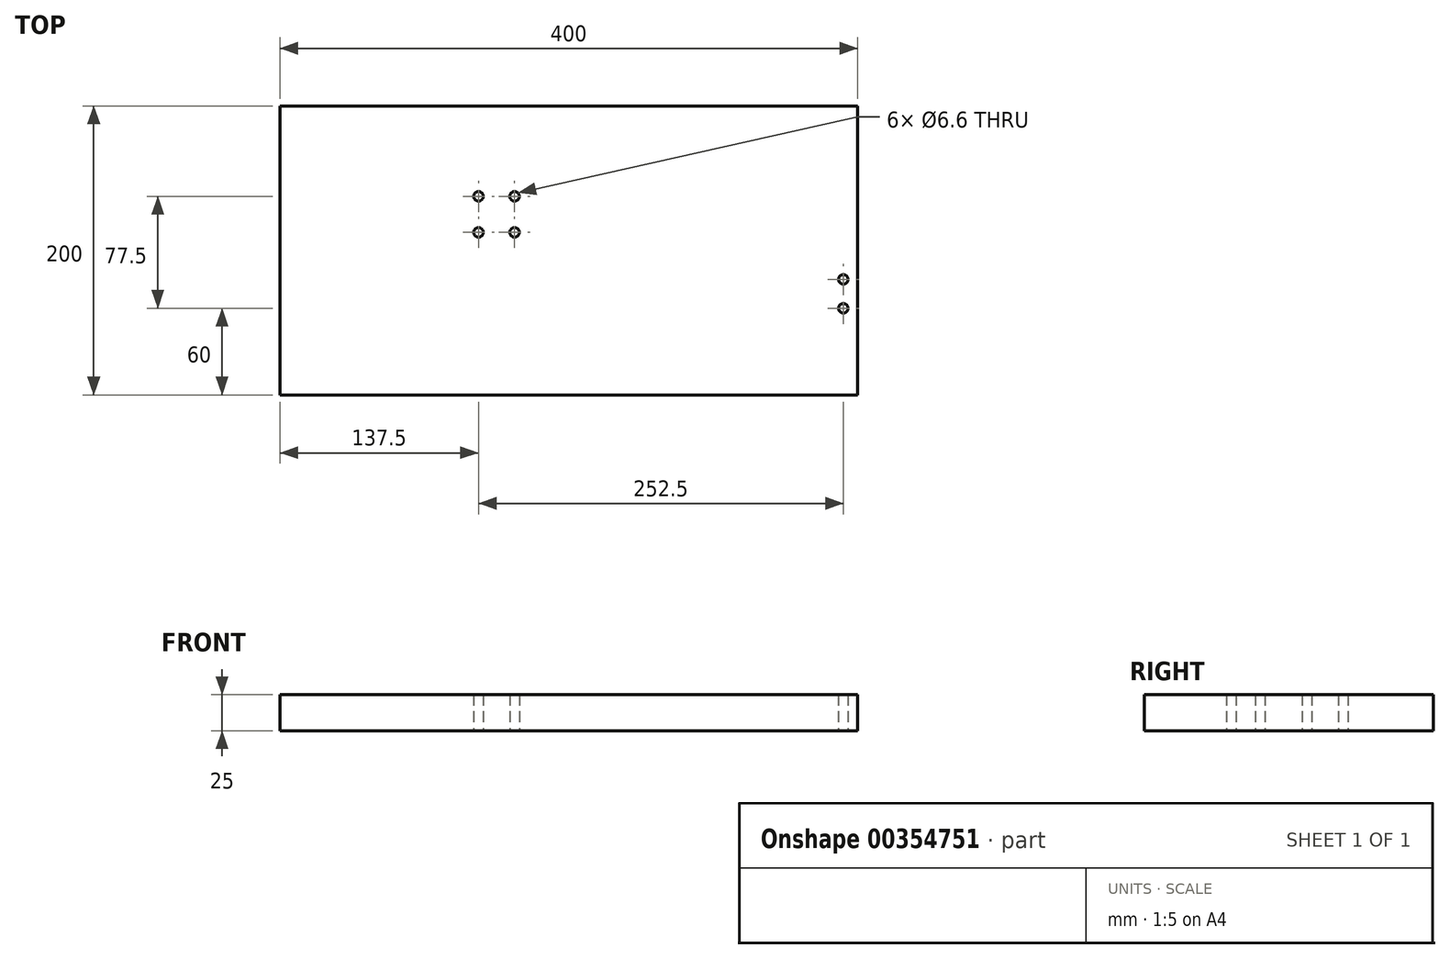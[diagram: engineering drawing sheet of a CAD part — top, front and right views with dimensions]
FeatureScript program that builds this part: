
annotation { "Feature Type Name" : "Feature", "Feature Type Description" : "" }
export const myFeature = defineFeature(function(context is Context, id is Id, definition is map)
    precondition{}
    {
        {
            var Q0;
            Q0=qCreatedBy(makeId("Top.planeOp"),FACE);
            var sketch = newSketch(context, id + "F0", { "sketchPlane" : qUnion([Q0])});
            skLineSegment(sketch, "E0.bottom", {"start": v(200, 100) * mm, "end": v(-200, 100) * mm});
            skLineSegment(sketch, "E0.top", {"start": v(200, -100) * mm, "end": v(-200, -100) * mm});
            skLineSegment(sketch, "E0.left", {"start": v(200, 100) * mm, "end": v(200, -100) * mm});
            skLineSegment(sketch, "E0.right", {"start": v(-200, 100) * mm, "end": v(-200, -100) * mm});
            skPoint(sketch, "E0.middle", {"position": v(0, 0) * mm});
            skPoint(sketch, "E1.endSnap0", {"position": v(0, 100) * mm});
            skLineSegment(sketch, "E2.bottom", {"start": v(-37.5, 37.5) * mm, "end": v(-62.5, 37.5) * mm});
            skLineSegment(sketch, "E2.top", {"start": v(-37.5, 12.5) * mm, "end": v(-62.5, 12.5) * mm});
            skLineSegment(sketch, "E2.left", {"start": v(-37.5, 37.5) * mm, "end": v(-37.5, 12.5) * mm});
            skLineSegment(sketch, "E2.right", {"start": v(-62.5, 37.5) * mm, "end": v(-62.5, 12.5) * mm});
            skPoint(sketch, "E2.middle", {"position": v(-50, 25) * mm});
            skLineSegment(sketch, "E3", {"start": v(190, -40) * mm, "end": v(190, -20) * mm});
            skSolve(sketch);
        }
        {
            var Q0;
            Q0 = qSketchRegion(id + "F0", true);
            var Q1;
            Q1=makeQuery(id+"F0.imprint","IMPRINT",FACE,{"disambiguationData":[TD([[makeQuery(id+"F0.imprint","IMPRINT",EDGE,{"derivedFrom":sQuery(id+"F0.wireOp",EDGE,"E2.bottom")}),1.0]])]});
            extrude(context, id + "F1", {"entities" : qUnion([Q0, Q1]), "depth" : 25 * mm});
        }
        {
            var Q0;
            Q0=sQuery(id+"F0.wireOp",VERTEX,"E2.bottom.end");
            var Q1;
            Q1=sQuery(id+"F0.wireOp",VERTEX,"E2.top.start");
            var Q2;
            Q2=sQuery(id+"F0.wireOp",VERTEX,"E2.left.start");
            var Q3;
            Q3=sQuery(id+"F0.wireOp",VERTEX,"E2.top.end");
            var Q4;
            Q4=makeQuery(id+"F1.opExtrude","SWEPT_BODY",BODY,{"disambiguationData":[OSD([sQuery(id+"F0.wireOp",EDGE,"E0.bottom"),sQuery(id+"F0.wireOp",EDGE,"E0.top"),sQuery(id+"F0.wireOp",EDGE,"E0.left"),sQuery(id+"F0.wireOp",EDGE,"E0.right")])]});
            hole(context, id + "F2", {"style" : HoleStyle.SIMPLE, "endStyle" : HoleEndStyle.BLIND, "oppositeDirection" : true, "standardTappedOrClearance" : lookupTablePath({ "standard" : "ISO", "fit" : "Normal", "size" : "M6", "type" : "Clearance" }), "standardBlindInLast" : lookupTablePath({ "fit" : "Standard", "standard" : "ISO", "size" : "M6", "type" : "Clearance" }), "holeDiameter" : 6.6 * mm, "holeDepth" : 25 * mm, "isTappedThrough" : true, "tappedDepth" : 12 * mm, "tapClearance" : 3, "startFromSketch" : true, "locations" : qUnion([Q0, Q1, Q2, Q3]), "scope" : qUnion([Q4])});
        }
        {
            var Q0;
            Q0=sQuery(id+"F0.wireOp",VERTEX,"E3.end");
            var Q1;
            Q1=sQuery(id+"F0.wireOp",VERTEX,"E3.start");
            var Q2;
            Q2=makeQuery(id+"F1.opExtrude","SWEPT_BODY",BODY,{"disambiguationData":[OSD([sQuery(id+"F0.wireOp",EDGE,"E0.bottom"),sQuery(id+"F0.wireOp",EDGE,"E0.top"),sQuery(id+"F0.wireOp",EDGE,"E0.left"),sQuery(id+"F0.wireOp",EDGE,"E0.right")])]});
            hole(context, id + "F3", {"style" : HoleStyle.SIMPLE, "endStyle" : HoleEndStyle.BLIND, "oppositeDirection" : true, "standardTappedOrClearance" : lookupTablePath({ "standard" : "ISO", "fit" : "Normal", "size" : "M6", "type" : "Clearance" }), "standardBlindInLast" : lookupTablePath({ "fit" : "Standard", "standard" : "ISO", "size" : "M6", "type" : "Clearance" }), "holeDiameter" : 6.6 * mm, "holeDepth" : 25 * mm, "isTappedThrough" : true, "tappedDepth" : 12 * mm, "tapClearance" : 3, "startFromSketch" : true, "locations" : qUnion([Q0, Q1]), "scope" : qUnion([Q2])});
        }
    });
